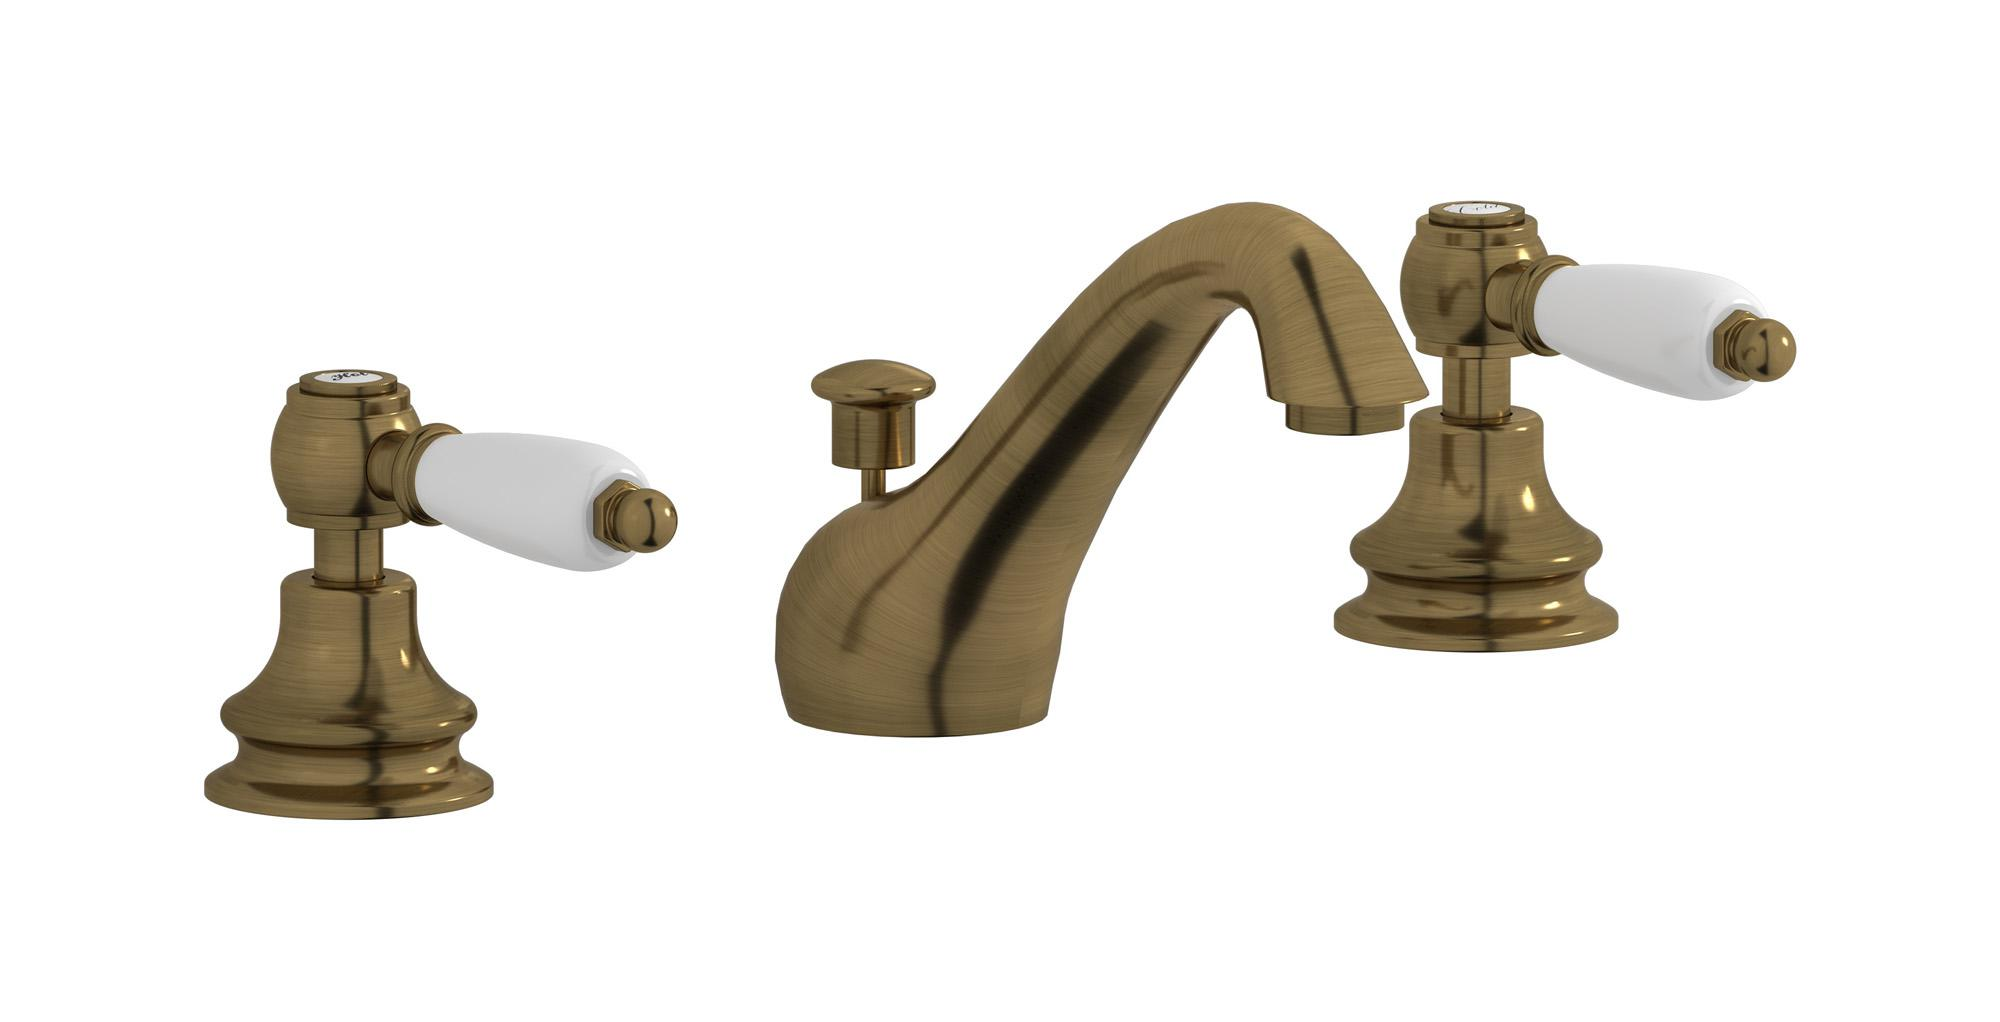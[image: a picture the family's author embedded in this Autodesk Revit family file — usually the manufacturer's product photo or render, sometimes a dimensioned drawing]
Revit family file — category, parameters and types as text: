
# Revit family: HL392_2
name_source: partatom
category: Apparecchi idraulici
units: mm (PartAtom-declared; Revit-internal decimal feet)

## family parameters
Basato su piano di lavoro = No
Condiviso = No
Mantieni orientamento annotazione = No
Numero OmniClass = 23.45.55.17
Punto di calcolo locali = No
Quota connettore circolare = Usa diametro
Sempre verticale = Sì
Taglio con vuoti quando caricato = No
Tipo di parte = Normale
Titolo OmniClass = Mixing Faucets

## types (8) — shared parameters
Cold water inlet = 10 mm  [stored 0.0328084 ft]
Commenti sul tipo = Three holes washbasin set with low spout
Connessione CW = No
Connessione HW = No
Connessione di scarico = No
Connessione di ventilazione = No
Descrizione = Three holes washbasin set with low spout
Hot water inlet = 10 mm  [stored 0.0328084 ft]
Produttore = IB Rubinetterie S.p.A.
URL = https://www.weareib.it
zero-valued in all types: Prospetto di default

## per-type parameters (varying)
| type | Finishes surface | Immagine tipo | Modello |
| Chrome | IB_Chrome | HL392CC_2.jpg | HL392CC_2 |
| Antique Bronze | IB_Antique bronze | HL392BB_2.jpg | HL392BB_2 |
| Pale Gold | IB_Pale gold | HL392II_2.jpg | HL392II_2 |
| Brushed Gold | IB_brushed gold | HL392OS_2.jpg | HL392OS_2 |
| Platinum | IB_Platinum | HL392PL_2.jpg | HL392PL_2 |
| Antique Copper | IB_Antique copper | HL392RR_2.jpg | HL392RR_2 |
| Rose Gold | IB_Rose gold | HL392RS_2.jpg | HL392RS_2 |
| Brushed Nickel | IB_Brushed nickel | HL392SS_2.jpg | HL392SS_2 |

note: [stored X ft] marks values corroborated as IEEE doubles in the binary element streams (Revit-internal decimal feet)
